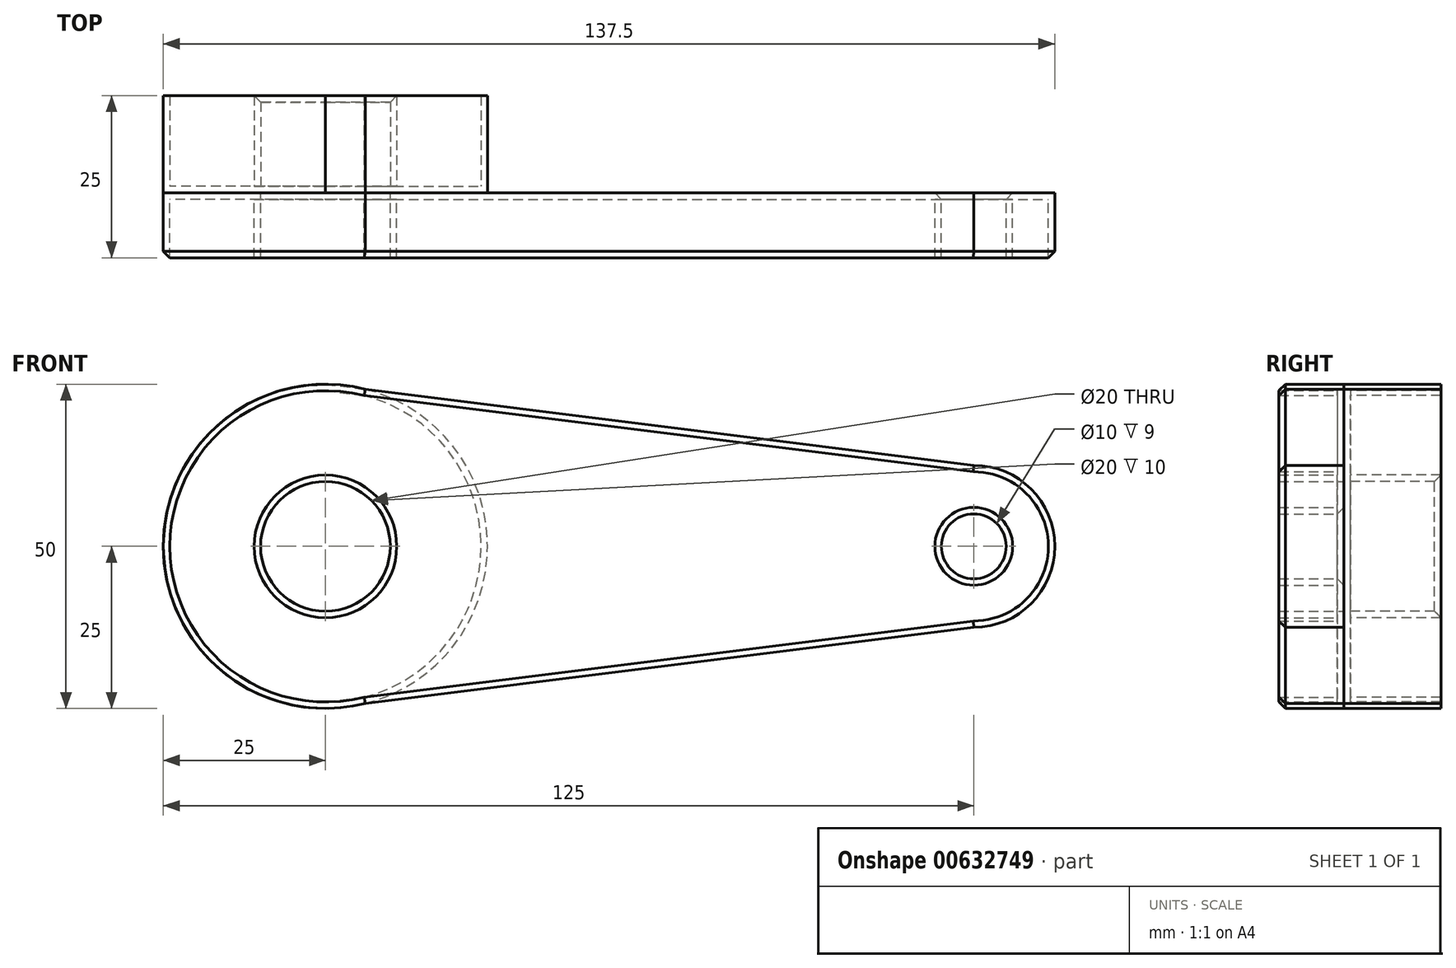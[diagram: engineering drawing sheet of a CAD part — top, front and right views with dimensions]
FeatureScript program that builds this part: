
annotation { "Feature Type Name" : "Feature", "Feature Type Description" : "" }
export const myFeature = defineFeature(function(context is Context, id is Id, definition is map)
    precondition{}
    {
        {
            var Q0;
            Q0=qCreatedBy(makeId("Front.planeOp"),FACE);
            var sketch = newSketch(context, id + "F0", { "sketchPlane" : qUnion([Q0])});
            skCircle(sketch, "E0", {"center": v(0, 0) * mm, "radius": 25 * mm});
            skCircle(sketch, "E1", {"center": v(100, 0) * mm, "radius": 12.5 * mm});
            skLineSegment(sketch, "E2", {"start": v(0, 25) * mm, "end": v(100, 12.5) * mm});
            skLineSegment(sketch, "E3", {"start": v(0, -25) * mm, "end": v(100, -12.5) * mm});
            skCircle(sketch, "E4", {"center": v(0, 0) * mm, "radius": 10 * mm});
            skCircle(sketch, "E5", {"center": v(100, 0) * mm, "radius": 5 * mm});
            skSolve(sketch);
        }
        {
            var Q0;
            Q0 = qSketchRegion(id + "F0", true);
            extrude(context, id + "F1", {"entities" : qUnion([Q0]), "depth" : 10 * mm, "offsetDistance" : 25 * mm});
        }
        {
            var Q0;
            Q0=makeQuery(id+"F0.imprint","IMPRINT",FACE,{"disambiguationData":[TD([[makeQuery(id+"F0.imprint","IMPRINT",EDGE,{"derivedFrom":sQuery(id+"F0.wireOp",EDGE,"E4")}),-1.0]])]});
            var Q1;
            Q1=sQuery(id+"F0.wireOp",EDGE,"E4");
            var Q2;
            Q2=sQuery(id+"F0.wireOp",EDGE,"E0");
            extrude(context, id + "F2", {"entities" : qUnion([Q0]), "surfaceEntities" : qUnion([Q1, Q2]), "oppositeDirection" : true, "depth" : 15 * mm, "offsetDistance" : 25 * mm});
        }
        {
            var Q0;
            Q0=makeQuery(id+"F1.opExtrude","CAP_FACE",FACE,{"disambiguationData":[OSD([sQuery(id+"F0.wireOp",EDGE,"E0"),sQuery(id+"F0.wireOp",EDGE,"E1"),sQuery(id+"F0.wireOp",EDGE,"E2"),sQuery(id+"F0.wireOp",EDGE,"E3"),sQuery(id+"F0.wireOp",EDGE,"E4"),sQuery(id+"F0.wireOp",EDGE,"E5")])],"isStart":false});
            var Q1;
            Q1=makeQuery(id+"F2.opExtrude","CAP_FACE",FACE,{"disambiguationData":[OSD([sQuery(id+"F0.wireOp",EDGE,"E0"),sQuery(id+"F0.wireOp",EDGE,"E2"),sQuery(id+"F0.wireOp",EDGE,"E3"),sQuery(id+"F0.wireOp",EDGE,"E4")])],"isStart":false});
            var Q2;
            Q2=makeQuery(id+"F2.opExtrude","SWEPT_BODY",BODY,{"disambiguationData":[OSD([sQuery(id+"F0.wireOp",EDGE,"E0"),sQuery(id+"F0.wireOp",EDGE,"E2"),sQuery(id+"F0.wireOp",EDGE,"E3"),sQuery(id+"F0.wireOp",EDGE,"E4")])]});
            var Q3;
            Q3=makeQuery(id+"F1.opExtrude","SWEPT_BODY",BODY,{"disambiguationData":[OSD([sQuery(id+"F0.wireOp",EDGE,"E0"),sQuery(id+"F0.wireOp",EDGE,"E1"),sQuery(id+"F0.wireOp",EDGE,"E2"),sQuery(id+"F0.wireOp",EDGE,"E3"),sQuery(id+"F0.wireOp",EDGE,"E4"),sQuery(id+"F0.wireOp",EDGE,"E5")])]});
            shell(context, id + "F3", {"entities" : qUnion([Q0, Q1]), "parts" : qUnion([Q2, Q3]), "thickness" : 1 * mm});
        }
        {
            var Q0;
            Q0=makeQuery(id+"F2.opExtrude","CAP_EDGE",EDGE,{"disambiguationData":[OSD([sQuery(id+"F0.wireOp",EDGE,"E4")])],"isStart":false});
            var Q1;
            Q1=makeQuery(id+"F1.opExtrude","CAP_EDGE",EDGE,{"disambiguationData":[OSD([sQuery(id+"F0.wireOp",EDGE,"E5")])],"isStart":true});
            var Q2;
            Q2=makeQuery(id+"F1.opExtrude","CAP_EDGE",EDGE,{"disambiguationData":[OSD([sQuery(id+"F0.wireOp",EDGE,"E2")])],"isStart":false});
            var Q3;
            Q3=makeQuery(id+"F1.opExtrude","CAP_EDGE",EDGE,{"disambiguationData":[OSD([sQuery(id+"F0.wireOp",EDGE,"E0")])],"isStart":false});
            var Q4;
            Q4=makeQuery(id+"F1.opExtrude","CAP_EDGE",EDGE,{"disambiguationData":[OSD([sQuery(id+"F0.wireOp",EDGE,"E3")])],"isStart":false});
            var Q5;
            Q5=makeQuery(id+"F1.opExtrude","CAP_EDGE",EDGE,{"disambiguationData":[OSD([sQuery(id+"F0.wireOp",EDGE,"E1")])],"isStart":false});
            chamfer(context, id + "F4", {"entities" : qUnion([Q0, Q1, Q2, Q3, Q4, Q5]), "width" : 1 * mm, "tangentPropagation" : true});
        }
    });
